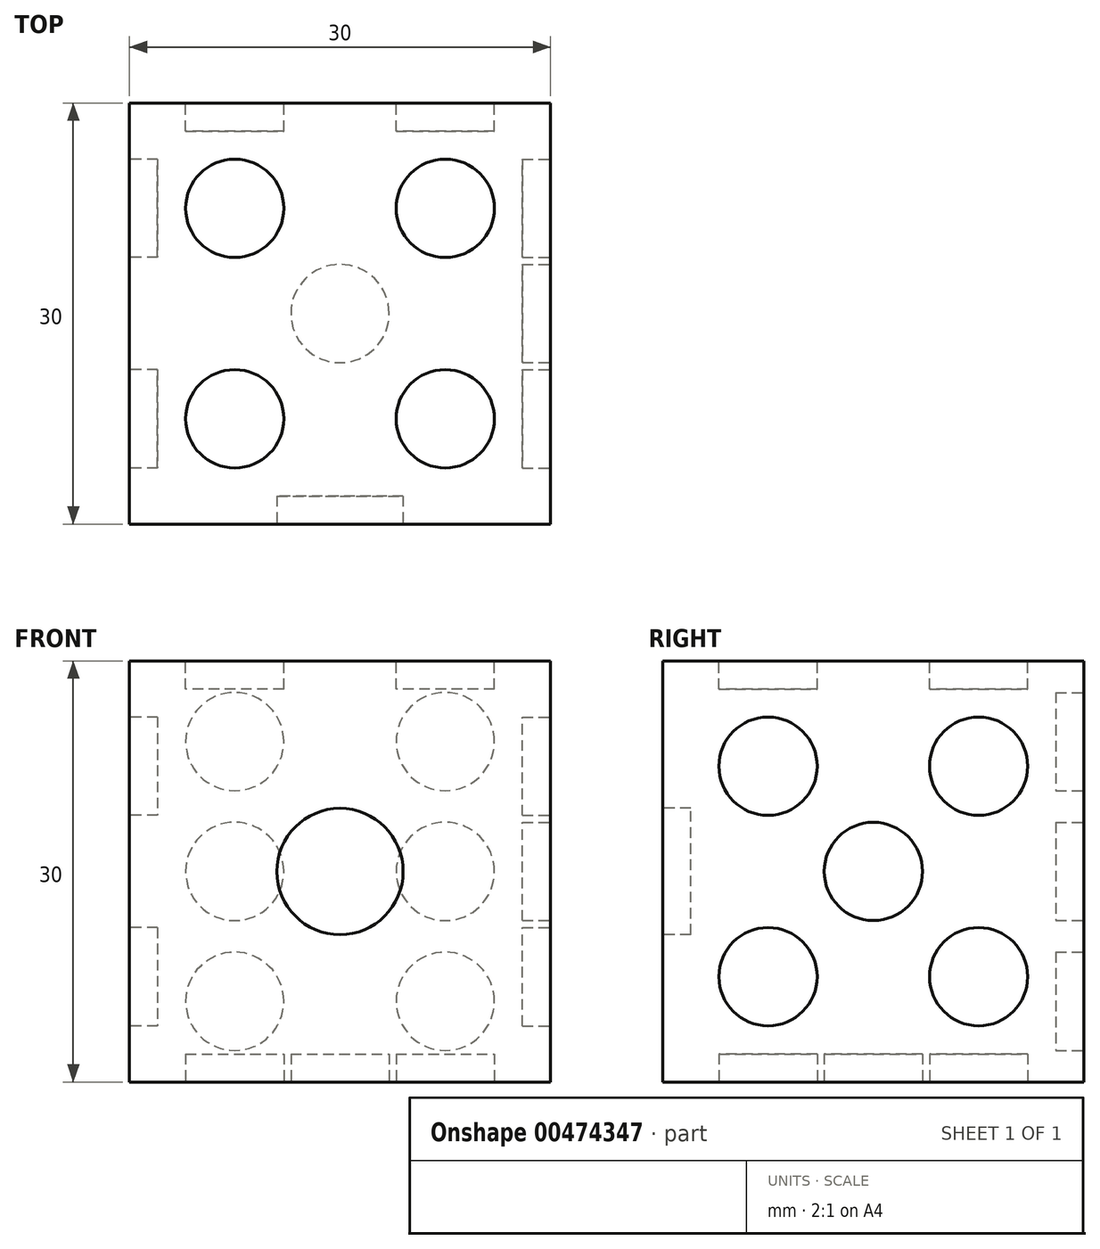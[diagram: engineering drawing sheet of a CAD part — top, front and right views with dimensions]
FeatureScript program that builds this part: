
annotation { "Feature Type Name" : "Feature", "Feature Type Description" : "" }
export const myFeature = defineFeature(function(context is Context, id is Id, definition is map)
    precondition{}
    {
        {
            var Q0;
            Q0=qCreatedBy(makeId("Front.planeOp"),FACE);
            var sketch = newSketch(context, id + "F0", { "sketchPlane" : qUnion([Q0])});
            skLineSegment(sketch, "E0.bottom", {"start": v(15, -15) * mm, "end": v(-15, -15) * mm});
            skLineSegment(sketch, "E0.top", {"start": v(15, 15) * mm, "end": v(-15, 15) * mm});
            skLineSegment(sketch, "E0.left", {"start": v(15, -15) * mm, "end": v(15, 15) * mm});
            skLineSegment(sketch, "E0.right", {"start": v(-15, -15) * mm, "end": v(-15, 15) * mm});
            skPoint(sketch, "E0.middle", {"position": v(0, 0) * mm});
            skSolve(sketch);
        }
        {
            var Q0;
            Q0 = qSketchRegion(id + "F0", true);
            extrude(context, id + "F1", {"entities" : qUnion([Q0]), "endBound" : BoundingType.SYMMETRIC, "depth" : 30 * mm});
        }
        {
            var Q0;
            Q0=makeQuery(id+"F1.opExtrude","CAP_FACE",FACE,{"disambiguationData":[OSD([sQuery(id+"F0.wireOp",EDGE,"E0.bottom"),sQuery(id+"F0.wireOp",EDGE,"E0.top"),sQuery(id+"F0.wireOp",EDGE,"E0.left"),sQuery(id+"F0.wireOp",EDGE,"E0.right")])],"isStart":false});
            var sketch = newSketch(context, id + "F2", { "sketchPlane" : qUnion([Q0])});
            skCircle(sketch, "E1", {"center": v(0, 0) * mm, "radius": 4.5 * mm});
            skSolve(sketch);
        }
        {
            var Q0;
            Q0 = qSketchRegion(id + "F2", true);
            extrude(context, id + "F3", {"entities" : qUnion([Q0]), "operationType" : NewBodyOperationType.REMOVE, "oppositeDirection" : true, "depth" : 2 * mm});
        }
        {
            var Q0;
            Q0=makeQuery(id+"F1.opExtrude","CAP_FACE",FACE,{"disambiguationData":[OSD([sQuery(id+"F0.wireOp",EDGE,"E0.bottom"),sQuery(id+"F0.wireOp",EDGE,"E0.top"),sQuery(id+"F0.wireOp",EDGE,"E0.left"),sQuery(id+"F0.wireOp",EDGE,"E0.right")])],"isStart":true});
            var sketch = newSketch(context, id + "F4", { "sketchPlane" : qUnion([Q0])});
            skLineSegment(sketch, "E2", {"start": v(-7.5, 14.44) * mm, "end": v(-7.5, -13.3) * mm});
            skCircle(sketch, "E3", {"center": v(-7.5, 0) * mm, "radius": 3.5 * mm});
            skCircle(sketch, "E4", {"center": v(-7.5, 9.25) * mm, "radius": 3.5 * mm});
            skCircle(sketch, "E5", {"center": v(-7.5, -9.25) * mm, "radius": 3.5 * mm});
            skSolve(sketch);
        }
        {
            var Q0;
            Q0=makeQuery(id+"F4.imprint","IMPRINT",FACE,{"disambiguationData":[TD([[makeQuery(id+"F4.imprint","IMPRINT",EDGE,{"derivedFrom":makeQuery(id+"F1.opExtrude","CAP_EDGE",EDGE,{"disambiguationData":[OSD([sQuery(id+"F0.wireOp",EDGE,"E0.bottom")])],"isStart":true})}),1.0]])]});
            var sketch = newSketch(context, id + "F5", { "sketchPlane" : qUnion([Q0])});
            skCircle(sketch, "E6.1", {"center": v(-7.5, 0) * mm, "radius": 3.5 * mm});
            skCircle(sketch, "E6.2", {"center": v(-7.5, 9.25) * mm, "radius": 3.5 * mm});
            skCircle(sketch, "E6.3", {"center": v(-7.5, -9.25) * mm, "radius": 3.5 * mm});
            skPoint(sketch, "E7.orphan", {"position": v(-7.5, 14.44) * mm});
            skPoint(sketch, "E6.0.end.orphan", {"position": v(-7.5, -13.3) * mm});
            skCircle(sketch, "E8.MirrorC", {"center": v(7.5, 0) * mm, "radius": 3.5 * mm});
            skPoint(sketch, "E9.MirrorP", {"position": v(7.5, -13.3) * mm});
            skCircle(sketch, "E10.MirrorC", {"center": v(7.5, -9.25) * mm, "radius": 3.5 * mm});
            skCircle(sketch, "E11.MirrorC", {"center": v(7.5, 9.25) * mm, "radius": 3.5 * mm});
            skSolve(sketch);
        }
        {
            var Q0;
            Q0 = qSketchRegion(id + "F5", true);
            extrude(context, id + "F6", {"entities" : qUnion([Q0]), "operationType" : NewBodyOperationType.REMOVE, "oppositeDirection" : true, "depth" : 2 * mm});
        }
        {
            var Q0;
            Q0=makeQuery(id+"F1.opExtrude","SWEPT_FACE",FACE,{"disambiguationData":[OSD([sQuery(id+"F0.wireOp",EDGE,"E0.top")])]});
            var sketch = newSketch(context, id + "F7", { "sketchPlane" : qUnion([Q0])});
            skCircle(sketch, "E12", {"center": v(-7.5, 7.5) * mm, "radius": 3.5 * mm});
            skCircle(sketch, "E13.MirrorC", {"center": v(7.5, 7.5) * mm, "radius": 3.5 * mm});
            skCircle(sketch, "E14.MirrorC", {"center": v(7.5, -7.5) * mm, "radius": 3.5 * mm});
            skCircle(sketch, "E15.MirrorC", {"center": v(-7.5, -7.5) * mm, "radius": 3.5 * mm});
            skSolve(sketch);
        }
        {
            var Q0;
            Q0 = qSketchRegion(id + "F7", true);
            extrude(context, id + "F8", {"entities" : qUnion([Q0]), "operationType" : NewBodyOperationType.REMOVE, "oppositeDirection" : true, "depth" : 2 * mm});
        }
        {
            var Q0;
            Q0=makeQuery(id+"F1.opExtrude","SWEPT_FACE",FACE,{"disambiguationData":[OSD([sQuery(id+"F0.wireOp",EDGE,"E0.bottom")])]});
            var sketch = newSketch(context, id + "F9", { "sketchPlane" : qUnion([Q0])});
            skCircle(sketch, "E16", {"center": v(0, 0) * mm, "radius": 3.5 * mm});
            skCircle(sketch, "E17", {"center": v(-7.5, -7.5) * mm, "radius": 3.5 * mm});
            skCircle(sketch, "E18", {"center": v(7.5, 7.5) * mm, "radius": 3.5 * mm});
            skSolve(sketch);
        }
        {
            var Q0;
            Q0 = qSketchRegion(id + "F9", true);
            extrude(context, id + "F10", {"entities" : qUnion([Q0]), "operationType" : NewBodyOperationType.REMOVE, "oppositeDirection" : true, "depth" : 2 * mm});
        }
        {
            var Q0;
            Q0=makeQuery(id+"F1.opExtrude","SWEPT_FACE",FACE,{"disambiguationData":[OSD([sQuery(id+"F0.wireOp",EDGE,"E0.left")])]});
            var sketch = newSketch(context, id + "F11", { "sketchPlane" : qUnion([Q0])});
            skCircle(sketch, "E19", {"center": v(-7.5, 7.5) * mm, "radius": 3.5 * mm});
            skCircle(sketch, "E20.MirrorC", {"center": v(7.5, 7.5) * mm, "radius": 3.5 * mm});
            skCircle(sketch, "E21.MirrorC", {"center": v(7.5, -7.5) * mm, "radius": 3.5 * mm});
            skCircle(sketch, "E22.MirrorC", {"center": v(-7.5, -7.5) * mm, "radius": 3.5 * mm});
            skCircle(sketch, "E23", {"center": v(0, 0) * mm, "radius": 3.5 * mm});
            skSolve(sketch);
        }
        {
            var Q0;
            Q0 = qSketchRegion(id + "F11", true);
            extrude(context, id + "F12", {"entities" : qUnion([Q0]), "operationType" : NewBodyOperationType.REMOVE, "oppositeDirection" : true, "depth" : 2 * mm});
        }
        {
            var Q0;
            Q0=makeQuery(id+"F1.opExtrude","SWEPT_FACE",FACE,{"disambiguationData":[OSD([sQuery(id+"F0.wireOp",EDGE,"E0.right")])]});
            var sketch = newSketch(context, id + "F13", { "sketchPlane" : qUnion([Q0])});
            skCircle(sketch, "E24", {"center": v(-7.5, -7.5) * mm, "radius": 3.5 * mm});
            skCircle(sketch, "E25", {"center": v(7.5, 7.5) * mm, "radius": 3.5 * mm});
            skSolve(sketch);
        }
        {
            var Q0;
            Q0 = qSketchRegion(id + "F13", true);
            extrude(context, id + "F14", {"entities" : qUnion([Q0]), "operationType" : NewBodyOperationType.REMOVE, "oppositeDirection" : true, "depth" : 2 * mm});
        }
    });
